SOLIDWORKS PART (.sldprt)
format: sldprt  version: not decoded by parser v0  size: 710,144 bytes
history: native  units: mm
features: sketch x8, plane x4, extrude x4, cut_extrude x4, fillet x4, boolean_combine x2, material x1 (+8 scaffold rows collapsed)
feature tree (35):
  scaffold x8  (default folders/planes/origin — collapsed)
  material  "Material <not specified>"
  plane  "Alzado"
  plane  "Planta"
  plane  "Vista lateral"
  sketch  "Croquis1"  dims[D1=40.0mm D2=40.0mm D3=20.0mm D4=20.0mm]
  extrude  "Extruir1"  Depth=9.2mm
  sketch  "Croquis2"  dims[D1=32.4mm D2=16.2mm D3=34.0mm D4=17.0mm D5=9.3mm D6=12.4mm D7=6.2mm D8=1.5mm D9=9.0mm D10=9.0mm]
  cut_extrude  "Cortar-Extruir1"  Depth=16.2mm
  fillet  "Redondeo1"  Radius=3mm
  fillet  "Redondeo2"  Radius=0.2mm
  sketch  "Croquis3"  dims[D1=27.2mm D2=2.3mm D3=13.6mm]
  cut_extrude  "Cortar-Extruir2"  Depth=58.2mm
  sketch  "Croquis4"  dims[D1=37.4mm D2=18.7mm]
  cut_extrude  "Cortar-Extruir3"  Depth=58.2mm
  fillet  "Redondeo3"  Radius=0.7mm
  plane  "Plano1"  Offset=1.5mm
  sketch  "Croquis5"  dims[D1=37.0mm D2=37.0mm D3=18.5mm D4=18.5mm]
  extrude  "Extruir2"  Depth=2.5mm
  fillet  "Redondeo4"  Radius=3mm
  sketch  "Croquis6"  dims[D1=1.8mm]
  extrude  "Extruir3"  Depth=12.4mm
  boolean_combine  "Combinar1"
  sketch  "Croquis7"  dims[c1.D1=5.0mm c1.D2=21.0mm c1.D3=2.5mm c1.D4=1.2mm c1.D5=~1.220142mm c2.D4=17.25mm c2.D5=18.9mm c2.D6=10.5mm]
  cut_extrude  "Cortar-Extruir4"  Depth=12.4mm
  sketch  "Croquis8"  dims[D5=0.79mm D1=1.6mm D2=5.0mm D3=2.5mm D4=0.8mm]
  extrude  "Extruir4"  Depth=8.4mm
  boolean_combine  "Combinar2"
decode coverage: 20 of 22 modeling features carry decoded parameters
note: ~ marks probable driven/reference dimensions
note: suppression state not decoded; provenance and decode notes live in map.json
